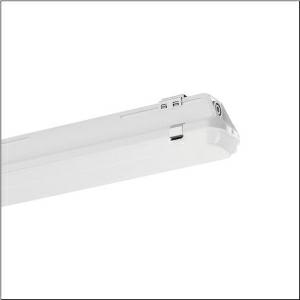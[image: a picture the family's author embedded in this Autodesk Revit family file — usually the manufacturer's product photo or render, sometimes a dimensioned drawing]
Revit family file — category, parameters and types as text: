
# Revit family: monsun_11_51fp107p460h
name_source: partatom
category: Lighting Fixtures
units: mm (PartAtom-declared; Revit-internal decimal feet)

## family parameters
Cut with Voids When Loaded = No
Host = Face
Light Source = No
Part Type = Normal
Room Calculation Point = No
Round Connector Dimension = Use Diameter
Shared = No

## types (1)
- Monsun 11 (1 x LED, 5800 lm, 32.5 W, 4000K)
    Apparent Load = 33 VA
    CIE Flux Codes = 47 77 93 94 100
    Color Rendering = 80
    Color Temperature = 4000K
    Default Elevation = 1800 mm
    Description = Monsun 11, damp-proof luminaire, chain hanger, primary optical cover: enclosure, of PMMA, light emission: direct distribution, primary light characteristic: symmetric, installation type: suspended mounting, surface-mounted, horizontal mounting, vertical mounting, LED, rated luminous flux: 5.800lm, luminous efficacy: 178lm/W, light colour: 840, colour temperature: 4000K, control gear: ON/OFF, with terminal, 3-pole, max. 2.5mm², mains connection: 220..240V, AC, 50/60Hz, rated input power: 33W, luminaire housing, of glass-fibre reinforced polyester, uncoated, bright grey, incl. chain hanger, length: 1.590mm, width: 90mm, height: 88mm, clip for enclosure, of stainless steel (V2A), ceiling mounting element, of stainless steel (V2A), chain hanger, of stainless steel (V2A), protection rating (complete): IP66, insulation class (complete): insulation class I (protective earthing), certification: CE, ENEC, VDE, UKCA, protection symbol: D, impact resistance: IK04, permissible operating ambient temperature: -35..+40°C, standard: EN 50419, EN 60598-2-1, no direct snow, no direct sun, no direct rain, for indoor or canopied outdoor use, corresponds to IFS (International Featured Standards) requirements for safety and quality in the food industry, contact your sales advisor before using the luminaires in applications with unclear chemical exposure, large temperature fluctuations or condensation-forming humidity, LABS conformity tested according to VDMA 24364:2018-05, packaging unit: 1 piece
    Height = 89 mm
    Lamp = 1 x LED
    Lamp Light Flux = 5800 lm
    Lamp Power = 32.5 W
    Lamp count = 1
    Length = 1590 mm
    Luminous efficacy = 178 lm/W
    Manufacturer = Siteco
    ModVariant = No
    Model = 51FP107P460H
    Mounting Place = Ceiling
    Mounting Type = Surface mounted
    Number of Poles = 1
    OnlyDefault = Yes
    Power Factor = 1
    Product Name = Monsun 11
    Product group = damp-proof luminaire
    ProductGroupID = 300
    Protection Class = Protection class I
    Protection Degree = IP 66
    RLX_Detail_Level = 1
    RLX_Emergency_Light_Flux = 0 lm
    RLX_Emergency_Type = 0
    RLX_Emergency_Type_DB = No
    RlxData = <blob elided: 88517 chars, md5=aacc485a>
    Socket = socket
    Standby Power = 0 W
    System Light Flux = 5800 lm
    System Power = 33 W
    Type Comments = Product without accessories
    Type Image = l_1349237.jpg
    URL = http://relux.com
    VarID = ---
    Voltage = 0 V
    Weight = 0.00 kg
    Width = 90 mm

## geometry (parser evidence)
native form markers: Blend x4, Sweep x12
no freeform markers — native parametric forms only
